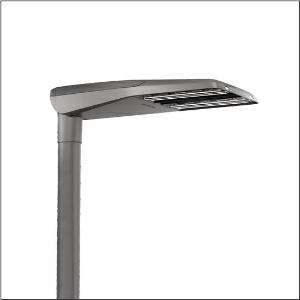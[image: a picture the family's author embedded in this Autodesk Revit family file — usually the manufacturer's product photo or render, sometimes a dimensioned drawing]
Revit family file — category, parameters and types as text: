
# Revit family: streetlight_sl_11_iq_midi___st1_2a_5xc3a51f08le_94b4
name_source: partatom
category: Lighting Fixtures
units: mm (PartAtom-declared; Revit-internal decimal feet)

## family parameters
Cut with Voids When Loaded = No
Host = Face
Light Source = No
Part Type = Normal
Room Calculation Point = No
Round Connector Dimension = Use Diameter
Shared = No

## types (1)
- --- (1 x LED, 9210 lm, 60.4 W, 3000K)
    Apparent Load = 60 VA
    CIE Flux Codes = 32 70 96 100 100
    Color Rendering = 70
    Color Temperature = 3000K
    Default Elevation = 1800 mm
    Description = Streetlight SL 11 iQ midi, mast luminaire, primary light control with 3 zone facetted reflector, of plastic, silver coated, highly specular, primary optical cover: cover, of PMMA, transparent, light distribution: ST1.2a, light emission: direct distribution, primary light characteristic: asymmetric, installation type: post-top, side-entry, LED, High Power LED, rated luminous flux: 9.210lm, luminous efficacy: 153lm/W, light colour: 730, colour temperature: 3000K, control: Street-Remote, optimised constant luminous flux control (CLO 2.0), Desk-Remote (wireless, voltage-free reading and setting of iQ features in the workshop via application-optimized NFC function/RFID function), Light-Fading, Smart-Wire, Night-Set, Lumen-Switch, Temp-Guard, Auto-Match, with cable H07RN-F 5x 1.5mm², mains connection: 230..240V, AC, 50/60Hz, connection cable pre-assembled, cable length: 8,5m, start of lifetime: 60W, end of service life: 63W, reduction: 30W, luminaire housing, of diecast aluminium, powder-coated, Siteco® metallic grey (DB 702S), please order mast flange separately, inclination adjustable without tools: 0°, 5°, 10°, 15° (post-top) | 0°, -5°, -10°, -15° (side-entry), sealing non-destructively replaceable, multi-level sealing system, length: 780mm, width: 376mm, height: 118mm, mast flange for spigot size: 42mm (side-entry): 5XC10008XM4, 60/48mm (side-entry/post-top): 5XC10108XM2, 76/60mm (side-entry/post-top): 5XC10108XM1, equipment: standard, protection rating (complete): IP66, insulation class (complete): insulation class II (safety insulation), certification: CE, ENEC, VDE, impact resistance: IK09, permissible operating ambient temperature for outdoor applications: -25..+50°C, standard-compliant lighting for roads and squares, Environmental Product Declaration (EPD) tested and certified by an independent institute, packaging unit: 1 piece

Light Distribution: ST1.2a
    Height = 118 mm
    Lamp = 1 x LED
    Lamp Light Flux = 9210 lm
    Lamp Power = 60.4 W
    Lamp count = 1
    Length = 780 mm
    Luminous efficacy = 152 lm/W
    Manufacturer = Siteco
    ModVariant = No
    Model = 5XC3A51F08LE
    Number of Poles = 1
    OnlyDefault = Yes
    Power Factor = 1
    Product Name = Streetlight SL 11 iQ midi | ST1.2a
    Product group = mast luminaire | pylon top
    ProductGroupID = 6100
    Protection Class = Protection class II
    Protection Degree = IP 66
    RLX_Detail_Level = 1
    RLX_Emergency_Light_Flux = 0 lm
    RLX_Emergency_Type = 0
    RLX_Emergency_Type_DB = No
    RlxData = <blob elided: 70733 chars, md5=42cdda8d>
    Socket = socket
    Standby Power = 0 W
    System Light Flux = 9210 lm
    System Power = 60 W
    Type Comments = factory setting: luminous flux: 100 % | dim-lin: 254 | 520 mA
    Type Image = l_1005960.jpg
    URL = http://relux.com
    VarID = @adj_150715
    Voltage = 0 V
    Weight = 0.00 kg
    Width = 376 mm

## geometry (parser evidence)
native form markers: Blend x4, Sweep x9
no freeform markers — native parametric forms only
